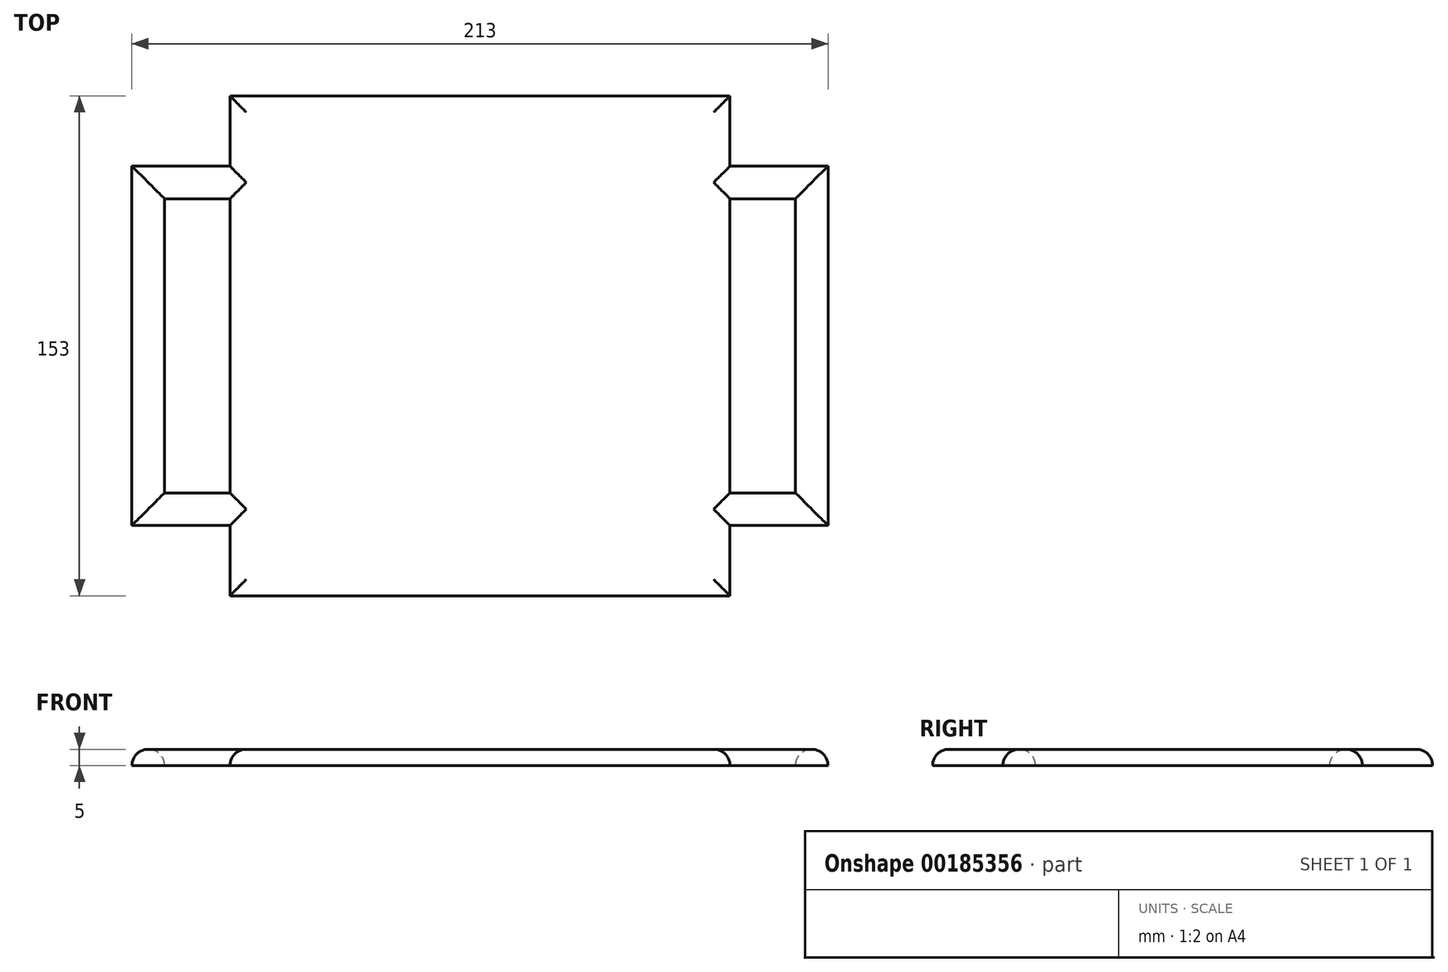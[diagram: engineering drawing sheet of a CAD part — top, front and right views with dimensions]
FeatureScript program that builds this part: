
annotation { "Feature Type Name" : "Feature", "Feature Type Description" : "" }
export const myFeature = defineFeature(function(context is Context, id is Id, definition is map)
    precondition{}
    {
        {
            assignVariable(context, id + "F0", {"name" : "StampThickness", "anyValue" : 5});
        }
        {
            var Q0;
            Q0=qCreatedBy(makeId("Top.planeOp"),FACE);
            var sketch = newSketch(context, id + "F1", { "sketchPlane" : qUnion([Q0])});
            skLineSegment(sketch, "E0.bottom", {"start": v(76.5, -76.5) * mm, "end": v(-76.5, -76.5) * mm});
            skLineSegment(sketch, "E0.top", {"start": v(76.5, 76.5) * mm, "end": v(-76.5, 76.5) * mm});
            skLineSegment(sketch, "E0.left", {"start": v(76.5, -76.5) * mm, "end": v(76.5, 76.5) * mm});
            skLineSegment(sketch, "E0.right", {"start": v(-76.5, -76.5) * mm, "end": v(-76.5, 76.5) * mm});
            skPoint(sketch, "E0.middle", {"position": v(0, 0) * mm});
            skLineSegment(sketch, "E1.bottom", {"start": v(-76.5, 55) * mm, "end": v(-106.5, 55) * mm});
            skLineSegment(sketch, "E1.top", {"start": v(-76.5, -55) * mm, "end": v(-106.5, -55) * mm});
            skLineSegment(sketch, "E1.left", {"start": v(-76.5, 55) * mm, "end": v(-76.5, -55) * mm});
            skLineSegment(sketch, "E1.right", {"start": v(-106.5, 55) * mm, "end": v(-106.5, -55) * mm});
            skLineSegment(sketch, "E2.MirrorCS", {"start": v(76.5, 55) * mm, "end": v(106.5, 55) * mm});
            skLineSegment(sketch, "E3.MirrorCS", {"start": v(106.5, 55) * mm, "end": v(106.5, -55) * mm});
            skLineSegment(sketch, "E4.MirrorCS", {"start": v(76.5, -55) * mm, "end": v(106.5, -55) * mm});
            skPoint(sketch, "E5", {"position": v(-106.5, 0) * mm});
            skPoint(sketch, "E6.oppositeSnap0", {"position": v(-91.5, 55) * mm});
            skLineSegment(sketch, "E6.bottom", {"start": v(-76.5, 45) * mm, "end": v(-96.5, 45) * mm});
            skLineSegment(sketch, "E6.top", {"start": v(-76.5, -45) * mm, "end": v(-96.5, -45) * mm});
            skLineSegment(sketch, "E6.left", {"start": v(-76.5, 45) * mm, "end": v(-76.5, -45) * mm});
            skLineSegment(sketch, "E6.right", {"start": v(-96.5, 45) * mm, "end": v(-96.5, -45) * mm});
            skPoint(sketch, "E7", {"position": v(-96.5, 0) * mm});
            skLineSegment(sketch, "E8.MirrorCS", {"start": v(96.5, 45) * mm, "end": v(96.5, -45) * mm});
            skLineSegment(sketch, "E9.MirrorCS", {"start": v(76.5, 45) * mm, "end": v(96.5, 45) * mm});
            skLineSegment(sketch, "E10.MirrorCS", {"start": v(76.5, -45) * mm, "end": v(96.5, -45) * mm});
            skSolve(sketch);
        }
        {
            var Q0;
            Q0=qSketchRegion(id+"F1",true);
            extrude(context, id + "F2", {"entities" : qUnion([Q0]), "depth" : (getVariable(context, 'StampThickness')) * mm, "offsetDistance" : 25 * mm});
        }
        {
            var Q0;
            Q0=makeQuery(id+"F2.opExtrude","CAP_FACE",FACE,{"disambiguationData":[OSD([sQuery(id+"F1.wireOp",EDGE,"E0.bottom"),sQuery(id+"F1.wireOp",EDGE,"E0.top"),sQuery(id+"F1.wireOp",EDGE,"E0.left"),sQuery(id+"F1.wireOp",EDGE,"E0.right"),sQuery(id+"F1.wireOp",EDGE,"E1.bottom"),sQuery(id+"F1.wireOp",EDGE,"E1.top"),sQuery(id+"F1.wireOp",EDGE,"E1.right"),sQuery(id+"F1.wireOp",EDGE,"2b3d4c0d-0223-475b-917f-fce990bc8d2c.0"),sQuery(id+"F1.wireOp",EDGE,"2b3d4c0d-0223-475b-917f-fce990bc8d2c.1"),sQuery(id+"F1.wireOp",EDGE,"2b3d4c0d-0223-475b-917f-fce990bc8d2c.2"),sQuery(id+"F1.wireOp",EDGE,"2b3d4c0d-0223-475b-917f-fce990bc8d2c.3"),sQuery(id+"F1.wireOp",EDGE,"E2.MirrorCS"),sQuery(id+"F1.wireOp",EDGE,"fab08b6f-8178-4721-a6eb-a873675159850.MirrorCS"),sQuery(id+"F1.wireOp",EDGE,"E3.MirrorCS"),sQuery(id+"F1.wireOp",EDGE,"6c955971-c0b2-4b58-bbc4-4c9c7526be6b0.MirrorCS"),sQuery(id+"F1.wireOp",EDGE,"3a808ee7-b43f-4b5e-9a05-6f0cd01ce6ac0.MirrorCS"),sQuery(id+"F1.wireOp",EDGE,"E4.MirrorCS"),sQuery(id+"F1.wireOp",EDGE,"bbff2cee-8e9e-45a7-b357-9ed76b106f360.MirrorCS")])],"isStart":false});
            fillet(context, id + "F3", {"entities" : qUnion([Q0]), "radius" : 5 * mm, "tangentPropagation" : true, "allowEdgeOverflow" : false});
        }
    });
